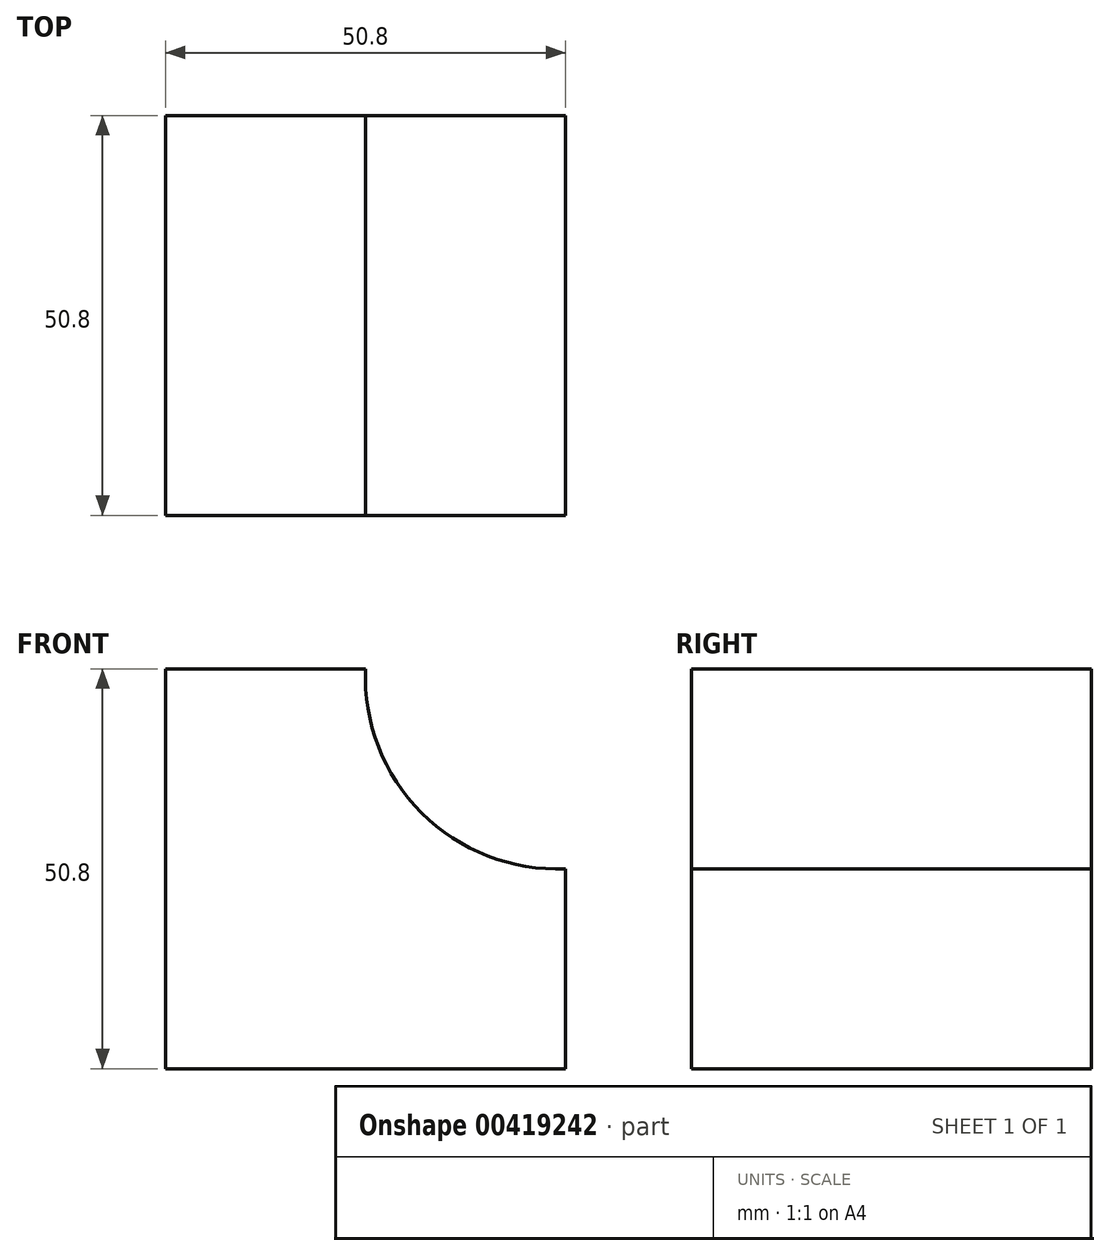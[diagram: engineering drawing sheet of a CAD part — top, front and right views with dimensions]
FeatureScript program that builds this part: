
annotation { "Feature Type Name" : "Feature", "Feature Type Description" : "" }
export const myFeature = defineFeature(function(context is Context, id is Id, definition is map)
    precondition{}
    {
        {
            var Q0;
            Q0=qCreatedBy(makeId("Front.planeOp"),FACE);
            var sketch = newSketch(context, id + "F0", { "sketchPlane" : qUnion([Q0])});
            skLineSegment(sketch, "E0", {"start": v(0, 0) * mm, "end": v(0, 50.8) * mm});
            skLineSegment(sketch, "E1", {"start": v(0, 50.8) * mm, "end": v(25.4, 50.8) * mm});
            skLineSegment(sketch, "E2", {"start": v(0, 0) * mm, "end": v(50.8, 0) * mm});
            skLineSegment(sketch, "E3", {"start": v(50.8, 0) * mm, "end": v(50.8, 25.4) * mm});
            skArc(sketch, "E4", {"start": v(25.4, 50.8) * mm, "mid": v(32.5, 32.5) * mm, "end": v(50.8, 25.4) * mm});
            skSolve(sketch);
        }
        {
            var Q0;
            Q0 = qSketchRegion(id + "F0", true);
            extrude(context, id + "F1", {"entities" : qUnion([Q0]), "depth" : 50.8 * mm});
        }
    });
